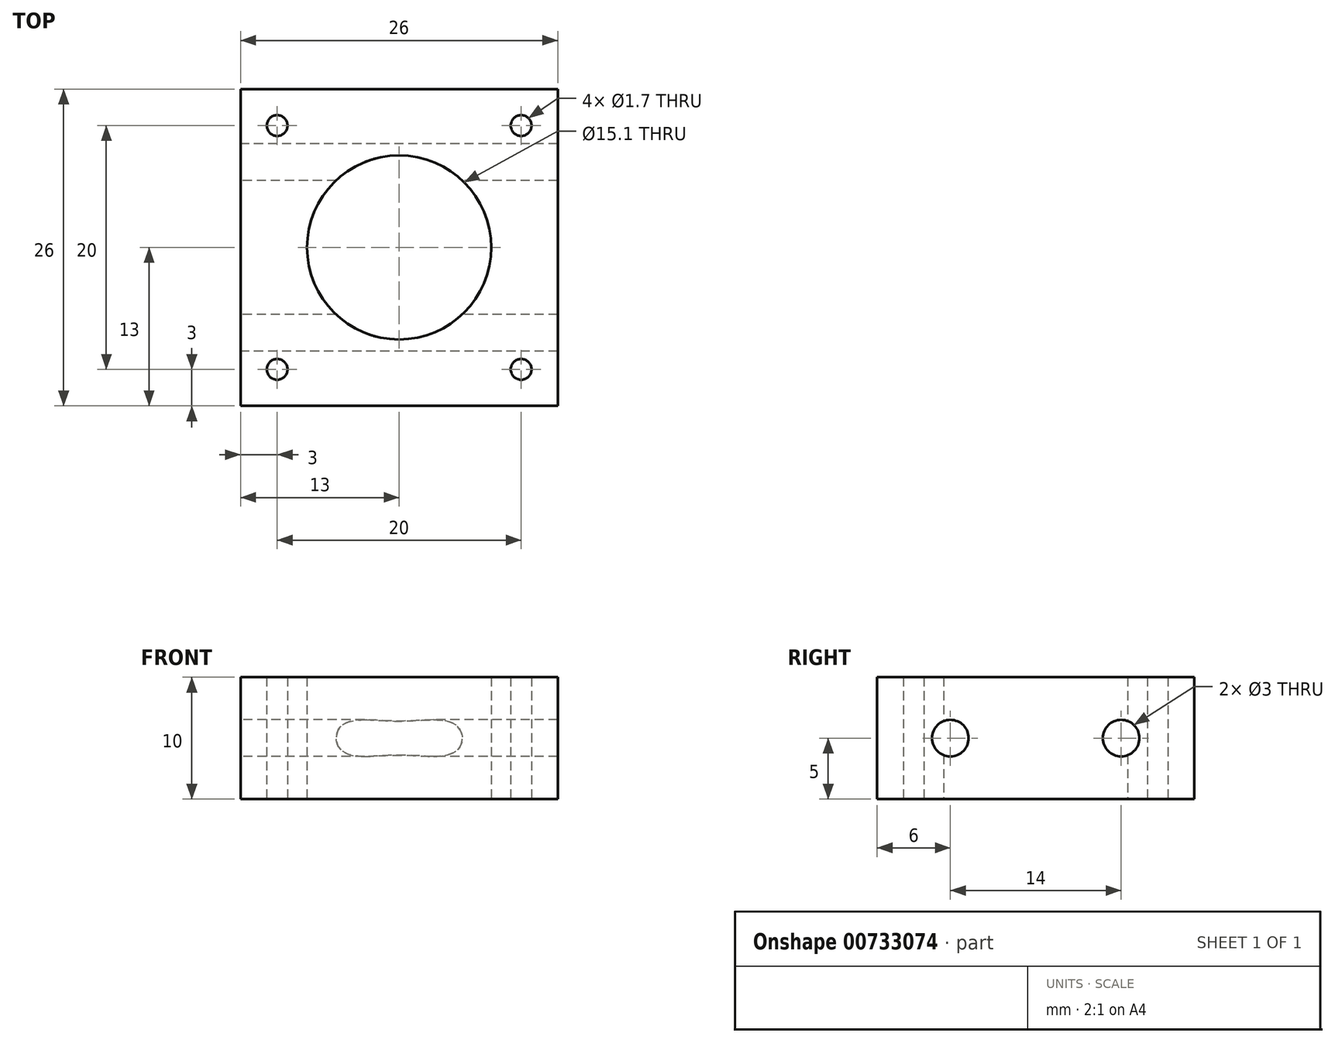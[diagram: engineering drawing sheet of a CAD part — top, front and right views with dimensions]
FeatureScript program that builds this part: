
annotation { "Feature Type Name" : "Feature", "Feature Type Description" : "" }
export const myFeature = defineFeature(function(context is Context, id is Id, definition is map)
    precondition{}
    {
        {
            var Q0;
            Q0=qCreatedBy(makeId("Top.planeOp"),FACE);
            var sketch = newSketch(context, id + "F0", { "sketchPlane" : qUnion([Q0])});
            skLineSegment(sketch, "E0.bottom", {"start": v(-13, 13) * mm, "end": v(13, 13) * mm});
            skLineSegment(sketch, "E0.top", {"start": v(-13, -13) * mm, "end": v(13, -13) * mm});
            skLineSegment(sketch, "E0.left", {"start": v(-13, 13) * mm, "end": v(-13, -13) * mm});
            skLineSegment(sketch, "E0.right", {"start": v(13, 13) * mm, "end": v(13, -13) * mm});
            skPoint(sketch, "E0.middle", {"position": v(0, 0) * mm});
            skCircle(sketch, "E1", {"center": v(0, 0) * mm, "radius": 7.55 * mm});
            skLineSegment(sketch, "E2.bottom", {"start": v(-10, 10) * mm, "end": v(10, 10) * mm, "construction": true});
            skLineSegment(sketch, "E2.top", {"start": v(-10, -10) * mm, "end": v(10, -10) * mm, "construction": true});
            skLineSegment(sketch, "E2.left", {"start": v(-10, 10) * mm, "end": v(-10, -10) * mm, "construction": true});
            skLineSegment(sketch, "E2.right", {"start": v(10, 10) * mm, "end": v(10, -10) * mm, "construction": true});
            skCircle(sketch, "E3", {"center": v(-10, 10) * mm, "radius": 0.85 * mm});
            skCircle(sketch, "E4.MirrorC", {"center": v(10, 10) * mm, "radius": 0.85 * mm});
            skCircle(sketch, "E5.MirrorC", {"center": v(-10, -10) * mm, "radius": 0.85 * mm});
            skCircle(sketch, "E6.MirrorC", {"center": v(10, -10) * mm, "radius": 0.85 * mm});
            skSolve(sketch);
        }
        {
            var Q0;
            Q0=qSketchRegion(id+"F0",true);
            extrude(context, id + "F1", {"entities" : qUnion([Q0]), "depth" : 10 * mm, "offsetDistance" : 25 * mm});
        }
        {
            var Q0;
            Q0=makeQuery(id+"F1.opExtrude","SWEPT_FACE",FACE,{"disambiguationData":[OSD([sQuery(id+"F0.wireOp",EDGE,"E0.left")])]});
            var sketch = newSketch(context, id + "F2", { "sketchPlane" : qUnion([Q0])});
            skLineSegment(sketch, "E7", {"start": v(-13, 5) * mm, "end": v(13, 5) * mm, "construction": true});
            skCircle(sketch, "E8", {"center": v(-7, 5) * mm, "radius": 1.5 * mm});
            skCircle(sketch, "E9.MirrorC", {"center": v(7, 5) * mm, "radius": 1.5 * mm});
            skSolve(sketch);
        }
        {
            var Q0;
            Q0=qSketchRegion(id+"F2",true);
            extrude(context, id + "F3", {"entities" : qUnion([Q0]), "operationType" : NewBodyOperationType.REMOVE, "endBound" : BoundingType.THROUGH_ALL, "oppositeDirection" : true, "depth" : 25 * mm, "offsetDistance" : 25 * mm});
        }
    });
